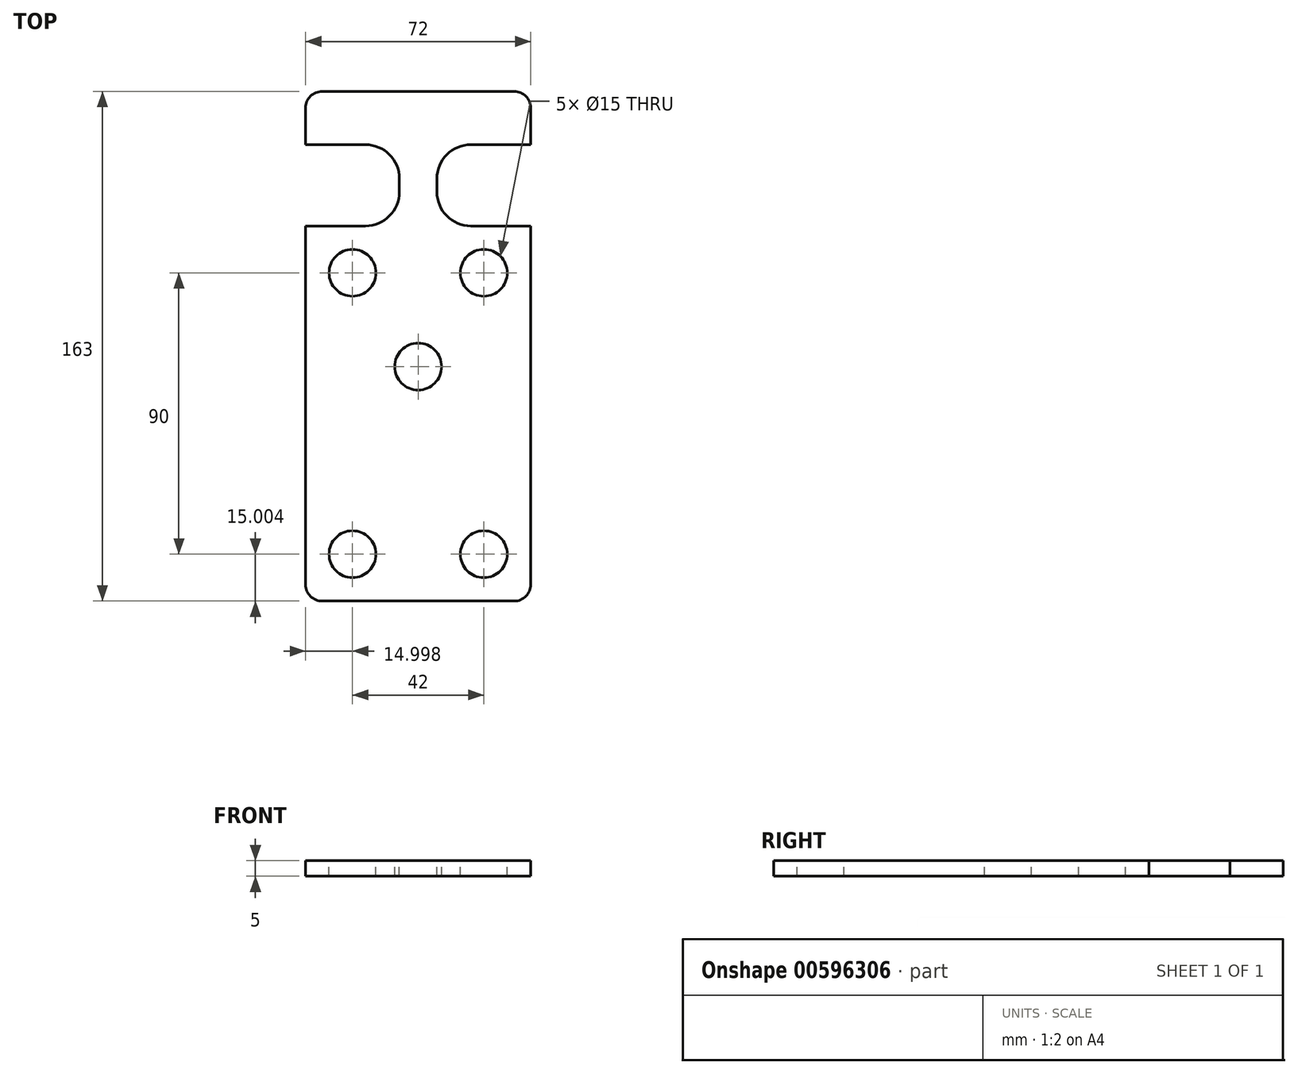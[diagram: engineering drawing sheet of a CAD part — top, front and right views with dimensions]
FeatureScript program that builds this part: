
annotation { "Feature Type Name" : "Feature", "Feature Type Description" : "" }
export const myFeature = defineFeature(function(context is Context, id is Id, definition is map)
    precondition{}
    {
        {
            var Q0;
            Q0=qCreatedBy(makeId("Top.planeOp"),FACE);
            var sketch = newSketch(context, id + "F0", { "sketchPlane" : qUnion([Q0])});
            skLineSegment(sketch, "E0.bottom", {"start": v(-44.34, 126.57) * mm, "end": v(27.66, 126.57) * mm});
            skLineSegment(sketch, "E0.top", {"start": v(-44.34, -36.43) * mm, "end": v(27.66, -36.43) * mm});
            skLineSegment(sketch, "E0.left", {"start": v(-44.34, 126.57) * mm, "end": v(-44.34, -36.43) * mm});
            skLineSegment(sketch, "E0.right", {"start": v(27.66, 126.57) * mm, "end": v(27.66, -36.43) * mm});
            skSolve(sketch);
        }
        {
            var Q0;
            Q0=qSketchRegion(id+"F0",true);
            extrude(context, id + "F1", {"entities" : qUnion([Q0]), "oppositeDirection" : true, "depth" : 5 * mm, "offsetDistance" : 25 * mm});
        }
        {
            var Q0;
            Q0=makeQuery(id+"F0.imprint","IMPRINT",FACE,{"disambiguationData":[TD([[makeQuery(id+"F0.imprint","IMPRINT",EDGE,{"derivedFrom":sQuery(id+"F0.wireOp",EDGE,"E0.bottom")}),-1.0]])]});
            var sketch = newSketch(context, id + "F2", { "sketchPlane" : qUnion([Q0])});
            skLineSegment(sketch, "E1.bottom", {"start": v(27.66, 109.57) * mm, "end": v(-2.34, 109.57) * mm});
            skLineSegment(sketch, "E1.top", {"start": v(27.66, 83.57) * mm, "end": v(-2.34, 83.57) * mm});
            skLineSegment(sketch, "E1.left", {"start": v(27.66, 109.57) * mm, "end": v(27.66, 83.57) * mm});
            skLineSegment(sketch, "E1.right", {"start": v(-2.34, 109.57) * mm, "end": v(-2.34, 83.57) * mm});
            skLineSegment(sketch, "E2.bottom", {"start": v(-44.34, 109.57) * mm, "end": v(-14.34, 109.57) * mm});
            skLineSegment(sketch, "E2.top", {"start": v(-44.34, 83.57) * mm, "end": v(-14.34, 83.57) * mm});
            skLineSegment(sketch, "E2.left", {"start": v(-44.34, 109.57) * mm, "end": v(-44.34, 83.57) * mm});
            skLineSegment(sketch, "E2.right", {"start": v(-14.34, 109.57) * mm, "end": v(-14.34, 83.57) * mm});
            skCircle(sketch, "E3", {"center": v(12.66, 68.57) * mm, "radius": 7.5 * mm});
            skCircle(sketch, "E4", {"center": v(-29.34, 68.57) * mm, "radius": 7.5 * mm});
            skCircle(sketch, "E5", {"center": v(-8.34, 38.57) * mm, "radius": 7.5 * mm});
            skCircle(sketch, "E6", {"center": v(-29.34, -21.43) * mm, "radius": 7.5 * mm});
            skCircle(sketch, "E7", {"center": v(12.66, -21.43) * mm, "radius": 7.5 * mm});
            skSolve(sketch);
        }
        {
            var Q0;
            Q0=qSketchRegion(id+"F2",true);
            extrude(context, id + "F3", {"entities" : qUnion([Q0]), "operationType" : NewBodyOperationType.REMOVE, "oppositeDirection" : true, "depth" : 25 * mm, "offsetDistance" : 25 * mm});
        }
        {
            var Q0;
            Q0=makeQuery(id+"F3.boolean.opBoolean","COPY",EDGE,{"derivedFrom":makeQuery(id+"F3.opExtrude","SWEPT_EDGE",EDGE,{"disambiguationData":[OSD([sQuery(id+"F2.wireOp",EDGE,"E1.bottom"),sQuery(id+"F2.wireOp",EDGE,"E1.right")])]})});
            var Q1;
            Q1=makeQuery(id+"F3.boolean.opBoolean","COPY",EDGE,{"derivedFrom":makeQuery(id+"F3.opExtrude","SWEPT_EDGE",EDGE,{"disambiguationData":[OSD([sQuery(id+"F2.wireOp",EDGE,"E1.top"),sQuery(id+"F2.wireOp",EDGE,"E1.right")])]})});
            var Q2;
            Q2=makeQuery(id+"F3.boolean.opBoolean","COPY",EDGE,{"derivedFrom":makeQuery(id+"F3.opExtrude","SWEPT_EDGE",EDGE,{"disambiguationData":[OSD([sQuery(id+"F2.wireOp",EDGE,"E2.top"),sQuery(id+"F2.wireOp",EDGE,"E2.right")])]})});
            var Q3;
            Q3=makeQuery(id+"F3.boolean.opBoolean","COPY",EDGE,{"derivedFrom":makeQuery(id+"F3.opExtrude","SWEPT_EDGE",EDGE,{"disambiguationData":[OSD([sQuery(id+"F2.wireOp",EDGE,"E2.bottom"),sQuery(id+"F2.wireOp",EDGE,"E2.right")])]})});
            fillet(context, id + "F4", {"entities" : qUnion([Q0, Q1, Q2, Q3]), "radius" : 10.86 * mm, "tangentPropagation" : true, "allowEdgeOverflow" : false});
        }
        {
            var Q0;
            Q0=makeQuery(id+"F1.opExtrude","SWEPT_EDGE",EDGE,{"disambiguationData":[OSD([sQuery(id+"F0.wireOp",EDGE,"E0.bottom"),sQuery(id+"F0.wireOp",EDGE,"E0.right")])]});
            var Q1;
            Q1=makeQuery(id+"F1.opExtrude","SWEPT_EDGE",EDGE,{"disambiguationData":[OSD([sQuery(id+"F0.wireOp",EDGE,"E0.bottom"),sQuery(id+"F0.wireOp",EDGE,"E0.left")])]});
            var Q2;
            Q2=makeQuery(id+"F3.boolean.opBoolean","COPY",EDGE,{"derivedFrom":makeQuery(id+"F3.opExtrude","SWEPT_EDGE",EDGE,{"disambiguationData":[OSD([sQuery(id+"F0.wireOp",EDGE,"E0.left"),sQuery(id+"F2.wireOp",EDGE,"E2.bottom"),sQuery(id+"F2.wireOp",EDGE,"E2.left")])]})});
            var Q3;
            Q3=makeQuery(id+"F3.boolean.opBoolean","COPY",EDGE,{"derivedFrom":makeQuery(id+"F3.opExtrude","SWEPT_EDGE",EDGE,{"disambiguationData":[OSD([sQuery(id+"F0.wireOp",EDGE,"E0.left"),sQuery(id+"F2.wireOp",EDGE,"E2.top"),sQuery(id+"F2.wireOp",EDGE,"E2.left")])]})});
            var Q4;
            Q4=makeQuery(id+"F3.boolean.opBoolean","COPY",EDGE,{"derivedFrom":makeQuery(id+"F3.opExtrude","SWEPT_EDGE",EDGE,{"disambiguationData":[OSD([sQuery(id+"F0.wireOp",EDGE,"E0.right"),sQuery(id+"F2.wireOp",EDGE,"E1.bottom"),sQuery(id+"F2.wireOp",EDGE,"E1.left")])]})});
            var Q5;
            Q5=makeQuery(id+"F3.boolean.opBoolean","COPY",EDGE,{"derivedFrom":makeQuery(id+"F3.opExtrude","SWEPT_EDGE",EDGE,{"disambiguationData":[OSD([sQuery(id+"F0.wireOp",EDGE,"E0.right"),sQuery(id+"F2.wireOp",EDGE,"E1.top"),sQuery(id+"F2.wireOp",EDGE,"E1.left")])]})});
            var Q6;
            Q6=makeQuery(id+"F1.opExtrude","SWEPT_EDGE",EDGE,{"disambiguationData":[OSD([sQuery(id+"F0.wireOp",EDGE,"E0.top"),sQuery(id+"F0.wireOp",EDGE,"E0.left")])]});
            var Q7;
            Q7=makeQuery(id+"F1.opExtrude","SWEPT_EDGE",EDGE,{"disambiguationData":[OSD([sQuery(id+"F0.wireOp",EDGE,"E0.top"),sQuery(id+"F0.wireOp",EDGE,"E0.right")])]});
            fillet(context, id + "F5", {"entities" : qUnion([Q0, Q1, Q2, Q3, Q4, Q5, Q6, Q7]), "radius" : 5.3 * mm, "tangentPropagation" : true, "allowEdgeOverflow" : false});
        }
    });
